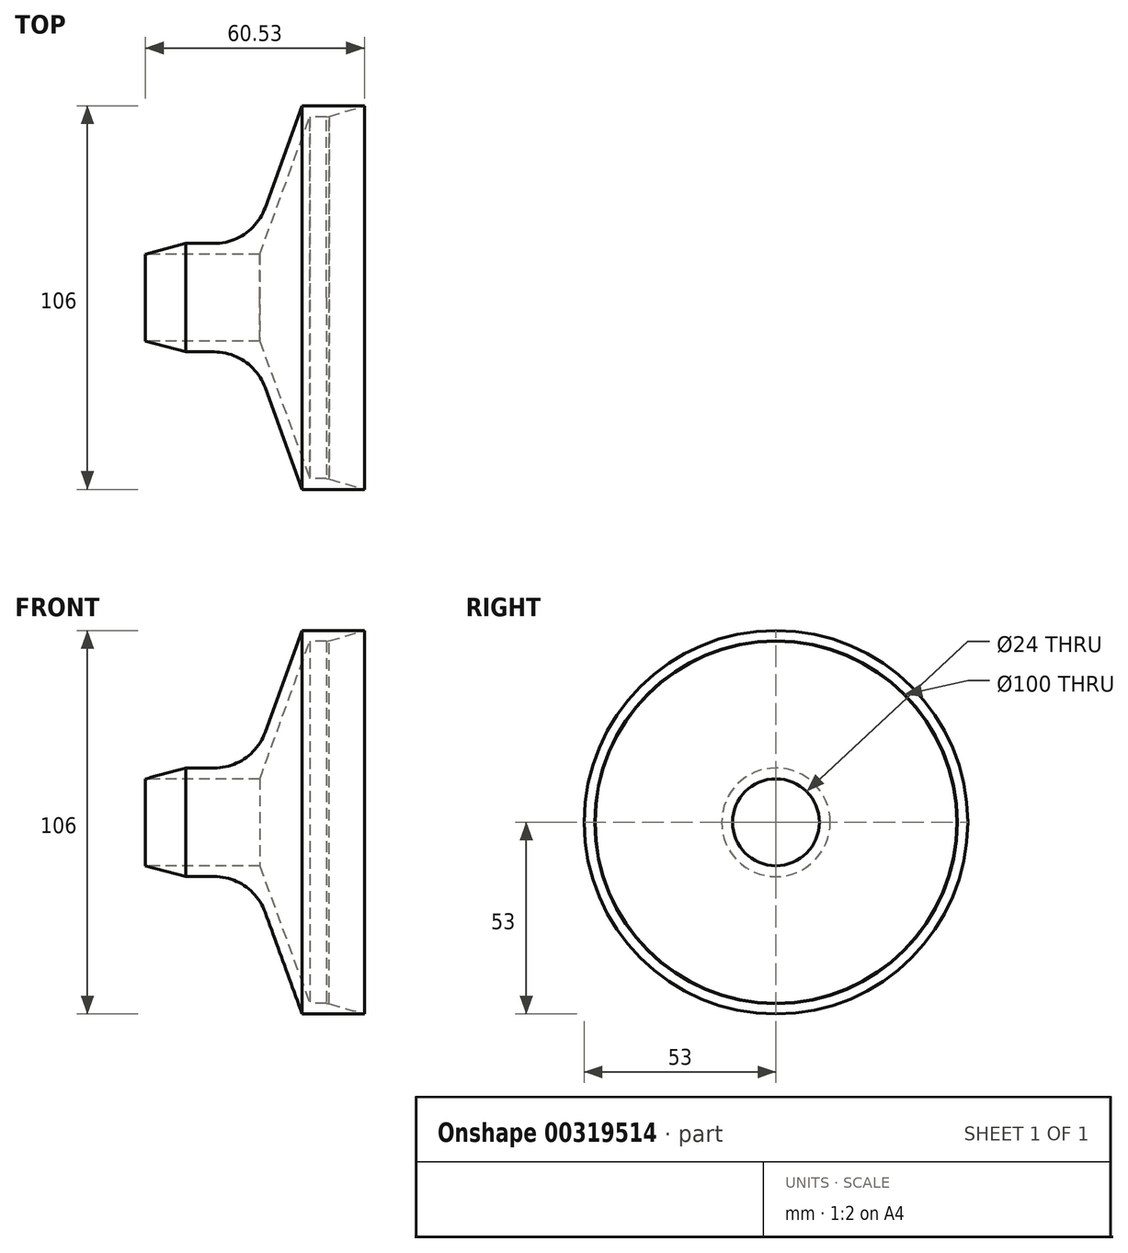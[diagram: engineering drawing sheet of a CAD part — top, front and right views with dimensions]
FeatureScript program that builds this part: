
annotation { "Feature Type Name" : "Feature", "Feature Type Description" : "" }
export const myFeature = defineFeature(function(context is Context, id is Id, definition is map)
    precondition{}
    {
        {
            var Q0;
            Q0=qCreatedBy(makeId("Front.planeOp"),FACE);
            var sketch = newSketch(context, id + "F0", { "sketchPlane" : qUnion([Q0])});
            skLineSegment(sketch, "E0", {"start": v(0, 0) * mm, "end": v(60, 0) * mm, "construction": true});
            skLineSegment(sketch, "E1", {"start": v(0, 0) * mm, "end": v(0, 12) * mm, "construction": true});
            skLineSegment(sketch, "E2", {"start": v(-11.6, 12) * mm, "end": v(0, 12) * mm});
            skLineSegment(sketch, "E3", {"start": v(0, 12) * mm, "end": v(0, 12) * mm});
            skLineSegment(sketch, "E4", {"start": v(0, 12) * mm, "end": v(20, 12) * mm});
            skLineSegment(sketch, "E5", {"start": v(20, 12) * mm, "end": v(33.83, 50) * mm});
            skLineSegment(sketch, "E6", {"start": v(33.83, 50) * mm, "end": v(38.83, 50) * mm});
            skLineSegment(sketch, "E7.0", {"start": v(31.73, 53) * mm, "end": v(48.94, 53) * mm});
            skLineSegment(sketch, "E7.1", {"start": v(17.9, 15) * mm, "end": v(31.73, 53) * mm});
            skLineSegment(sketch, "E7.2", {"start": v(-0.4, 15) * mm, "end": v(17.9, 15) * mm});
            skLineSegment(sketch, "E7.3", {"start": v(-11.6, 12) * mm, "end": v(-0.4, 15) * mm});
            skLineSegment(sketch, "E8", {"start": v(48.94, 53) * mm, "end": v(38.83, 50) * mm});
            skSolve(sketch);
        }
        {
            var Q0;
            Q0=makeQuery(id+"F0.imprint","IMPRINT",FACE,{"disambiguationData":[TD([[makeQuery(id+"F0.imprint","IMPRINT",EDGE,{"derivedFrom":sQuery(id+"F0.wireOp",EDGE,"E2")}),1.0]])]});
            var Q1;
            Q1=sQuery(id+"F0.wireOp",EDGE,"E0");
            revolve(context, id + "F1", {"entities" : qUnion([Q0]), "axis" : qUnion([Q1]), "revolveType" : RevolveType.FULL});
        }
        {
            var Q0;
            Q0=makeQuery(id+"F1.opRevolve","SWEPT_EDGE",EDGE,{"disambiguationData":[OSD([sQuery(id+"F0.wireOp",EDGE,"E6"),sQuery(id+"F0.wireOp",EDGE,"E8")])]});
            chamfer(context, id + "F2", {"entities" : qUnion([Q0]), "width" : 3 * mm, "tangentPropagation" : true});
        }
        {
            var Q0;
            Q0=makeQuery(id+"F1.opRevolve","SWEPT_EDGE",EDGE,{"disambiguationData":[OSD([sQuery(id+"F0.wireOp",EDGE,"E7.1"),sQuery(id+"F0.wireOp",EDGE,"E7.2")])]});
            fillet(context, id + "F3", {"entities" : qUnion([Q0]), "radius" : 15 * mm, "tangentPropagation" : true, "allowEdgeOverflow" : false});
        }
    });
